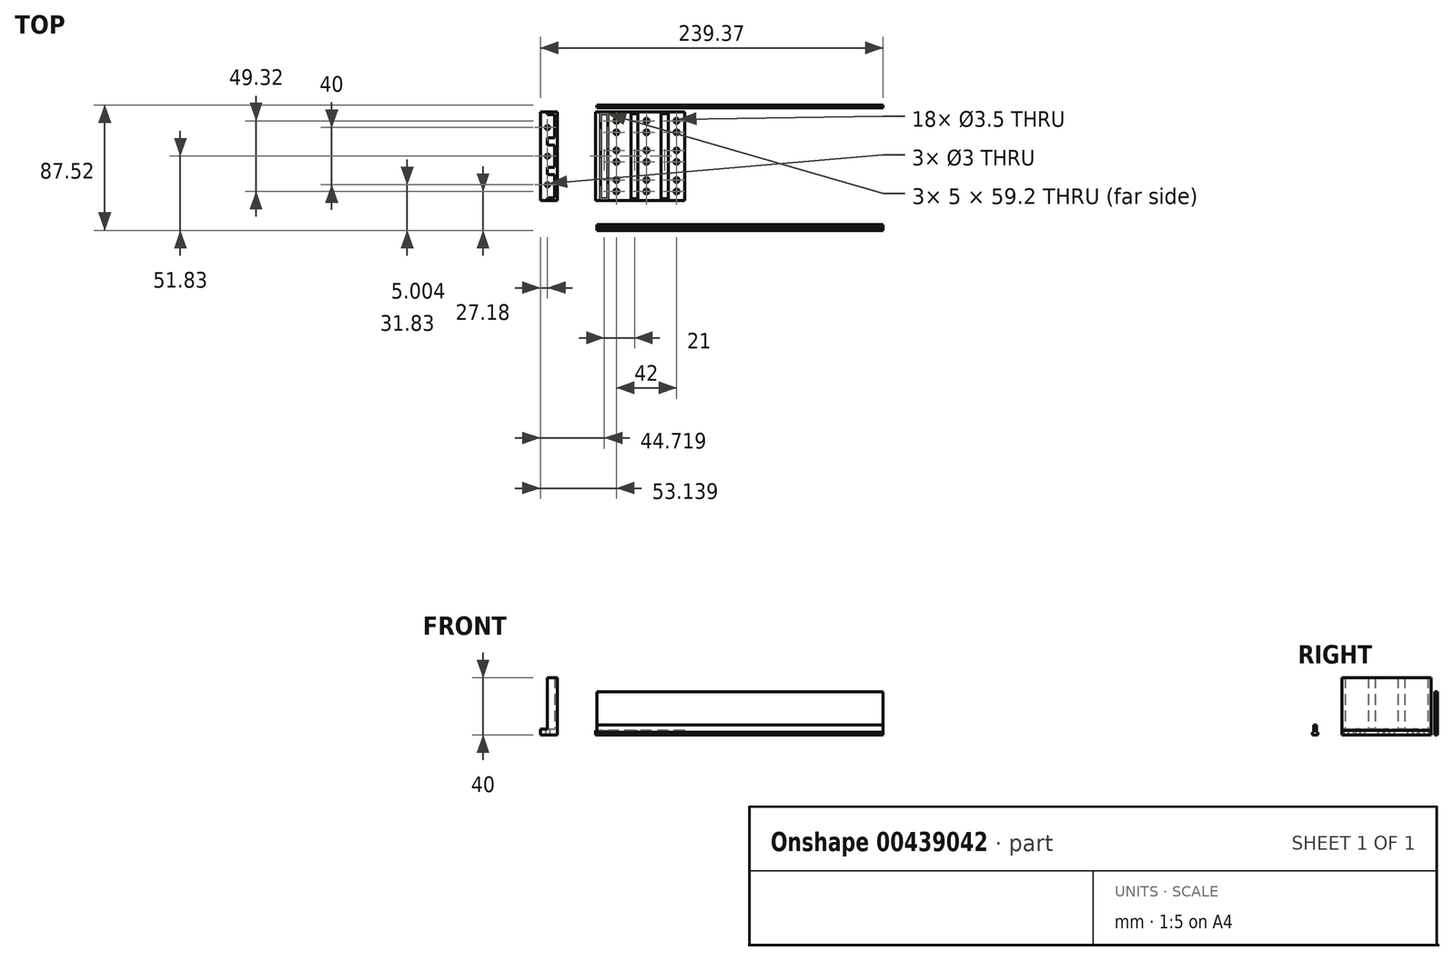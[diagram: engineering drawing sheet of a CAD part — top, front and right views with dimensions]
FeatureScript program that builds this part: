
annotation { "Feature Type Name" : "Feature", "Feature Type Description" : "" }
export const myFeature = defineFeature(function(context is Context, id is Id, definition is map)
    precondition{}
    {
        {
            var Q0;
            Q0=qCreatedBy(makeId("Top.planeOp"),FACE);
            var sketch = newSketch(context, id + "F0", { "sketchPlane" : qUnion([Q0])});
            skLineSegment(sketch, "E0.bottom", {"start": v(-38.73, -31) * mm, "end": v(-100.73, -31) * mm});
            skLineSegment(sketch, "E0.top", {"start": v(-38.73, 31) * mm, "end": v(-100.73, 31) * mm});
            skLineSegment(sketch, "E0.left", {"start": v(-38.73, -31) * mm, "end": v(-38.73, 31) * mm});
            skLineSegment(sketch, "E0.right", {"start": v(-100.73, -31) * mm, "end": v(-100.73, 31) * mm});
            skPoint(sketch, "E0.middle", {"position": v(-69.73, 0) * mm});
            skSolve(sketch);
        }
        {
            var Q0;
            Q0=qSketchRegion(id+"F0",true);
            extrude(context, id + "F1", {"entities" : qUnion([Q0]), "depth" : 3 * mm});
        }
        {
            var Q0;
            Q0=makeQuery(id+"F1.opExtrude","CAP_FACE",FACE,{"disambiguationData":[OSD([sQuery(id+"F0.wireOp",EDGE,"E0.bottom"),sQuery(id+"F0.wireOp",EDGE,"E0.top"),sQuery(id+"F0.wireOp",EDGE,"E0.left"),sQuery(id+"F0.wireOp",EDGE,"E0.right")])],"isStart":false});
            var sketch = newSketch(context, id + "F2", { "sketchPlane" : qUnion([Q0])});
            skCircle(sketch, "E1", {"center": v(-86.23, 24.67) * mm, "radius": 1.75 * mm});
            skCircle(sketch, "E2", {"center": v(-86.23, 16.67) * mm, "radius": 1.75 * mm});
            skCircle(sketch, "E3.0.1.0", {"center": v(-86.23, 4) * mm, "radius": 1.75 * mm});
            skCircle(sketch, "E3.0.1.1", {"center": v(-86.23, -4) * mm, "radius": 1.75 * mm});
            skCircle(sketch, "E3.0.2.0", {"center": v(-86.23, -16.65) * mm, "radius": 1.75 * mm});
            skCircle(sketch, "E3.0.2.1", {"center": v(-86.23, -24.65) * mm, "radius": 1.75 * mm});
            skCircle(sketch, "E3.1.0.0", {"center": v(-65.23, 24.67) * mm, "radius": 1.75 * mm});
            skCircle(sketch, "E3.1.0.1", {"center": v(-65.23, 16.67) * mm, "radius": 1.75 * mm});
            skCircle(sketch, "E3.1.1.0", {"center": v(-65.23, 4) * mm, "radius": 1.75 * mm});
            skCircle(sketch, "E3.1.1.1", {"center": v(-65.23, -4) * mm, "radius": 1.75 * mm});
            skCircle(sketch, "E3.1.2.0", {"center": v(-65.23, -16.65) * mm, "radius": 1.75 * mm});
            skCircle(sketch, "E3.1.2.1", {"center": v(-65.23, -24.65) * mm, "radius": 1.75 * mm});
            skCircle(sketch, "E3.2.0.0", {"center": v(-44.23, 24.67) * mm, "radius": 1.75 * mm});
            skCircle(sketch, "E3.2.0.1", {"center": v(-44.23, 16.67) * mm, "radius": 1.75 * mm});
            skCircle(sketch, "E3.2.1.0", {"center": v(-44.23, 4) * mm, "radius": 1.75 * mm});
            skCircle(sketch, "E3.2.1.1", {"center": v(-44.23, -4) * mm, "radius": 1.75 * mm});
            skCircle(sketch, "E3.2.2.0", {"center": v(-44.23, -16.65) * mm, "radius": 1.75 * mm});
            skCircle(sketch, "E3.2.2.1", {"center": v(-44.23, -24.65) * mm, "radius": 1.75 * mm});
            skLineSegment(sketch, "E3.direction1", {"start": v(-86.23, 16.67) * mm, "end": v(-65.23, 16.67) * mm, "construction": true});
            skLineSegment(sketch, "E3.direction2", {"start": v(-86.23, 16.67) * mm, "end": v(-86.23, -4) * mm, "construction": true});
            skLineSegment(sketch, "E4.bottom", {"start": v(-97.15, 29.6) * mm, "end": v(-92.15, 29.6) * mm});
            skLineSegment(sketch, "E4.top", {"start": v(-97.15, -29.6) * mm, "end": v(-92.15, -29.6) * mm});
            skLineSegment(sketch, "E4.left", {"start": v(-97.15, 29.6) * mm, "end": v(-97.15, -29.6) * mm});
            skLineSegment(sketch, "E4.right", {"start": v(-92.15, 29.6) * mm, "end": v(-92.15, -29.6) * mm});
            skLineSegment(sketch, "E5.1.0.0", {"start": v(-76.15, -29.6) * mm, "end": v(-71.15, -29.6) * mm});
            skLineSegment(sketch, "E5.1.0.1", {"start": v(-76.15, 29.6) * mm, "end": v(-71.15, 29.6) * mm});
            skLineSegment(sketch, "E5.1.0.2", {"start": v(-76.15, 29.6) * mm, "end": v(-76.15, -29.6) * mm});
            skLineSegment(sketch, "E5.1.0.3", {"start": v(-71.15, 29.6) * mm, "end": v(-71.15, -29.6) * mm});
            skLineSegment(sketch, "E5.2.0.0", {"start": v(-55.15, -29.6) * mm, "end": v(-50.15, -29.6) * mm});
            skLineSegment(sketch, "E5.2.0.1", {"start": v(-55.15, 29.6) * mm, "end": v(-50.15, 29.6) * mm});
            skLineSegment(sketch, "E5.2.0.2", {"start": v(-55.15, 29.6) * mm, "end": v(-55.15, -29.6) * mm});
            skLineSegment(sketch, "E5.2.0.3", {"start": v(-50.15, 29.6) * mm, "end": v(-50.15, -29.6) * mm});
            skLineSegment(sketch, "E5.direction1", {"start": v(-97.15, -29.6) * mm, "end": v(-76.15, -29.6) * mm, "construction": true});
            skSolve(sketch);
        }
        {
            var Q0;
            Q0=qSketchRegion(id+"F2",true);
            extrude(context, id + "F3", {"entities" : qUnion([Q0]), "operationType" : NewBodyOperationType.REMOVE, "oppositeDirection" : true, "depth" : 25 * mm});
        }
        {
            var Q0;
            Q0=qCreatedBy(makeId("Top.planeOp"),FACE);
            var sketch = newSketch(context, id + "F4", { "sketchPlane" : qUnion([Q0])});
            skLineSegment(sketch, "E6.bottom", {"start": v(-129.37, -31) * mm, "end": v(-139.37, -31) * mm});
            skLineSegment(sketch, "E6.top", {"start": v(-129.37, 31) * mm, "end": v(-139.37, 31) * mm});
            skLineSegment(sketch, "E6.left", {"start": v(-129.37, -31) * mm, "end": v(-129.37, 31) * mm});
            skLineSegment(sketch, "E6.right", {"start": v(-139.37, -31) * mm, "end": v(-139.37, 31) * mm});
            skPoint(sketch, "E6.middle", {"position": v(-134.37, 0) * mm});
            skCircle(sketch, "E7", {"center": v(-134.37, 20) * mm, "radius": 1.5 * mm});
            skCircle(sketch, "E8", {"center": v(-134.37, 0) * mm, "radius": 1.5 * mm});
            skCircle(sketch, "E9", {"center": v(-134.37, -20) * mm, "radius": 1.5 * mm});
            skSolve(sketch);
        }
        {
            var Q0;
            Q0=qSketchRegion(id+"F4",true);
            extrude(context, id + "F5", {"entities" : qUnion([Q0]), "depth" : 4 * mm});
        }
        {
            var Q0;
            Q0=qCreatedBy(makeId("Top.planeOp"),FACE);
            var sketch = newSketch(context, id + "F6", { "sketchPlane" : qUnion([Q0])});
            skLineSegment(sketch, "E10.bottom", {"start": v(-127.37, -31) * mm, "end": v(-129.37, -31) * mm});
            skLineSegment(sketch, "E10.top", {"start": v(-127.37, 31) * mm, "end": v(-129.37, 31) * mm});
            skLineSegment(sketch, "E10.left", {"start": v(-127.37, -31) * mm, "end": v(-127.37, 31) * mm});
            skLineSegment(sketch, "E10.right", {"start": v(-129.37, -31) * mm, "end": v(-129.37, 31) * mm});
            skPoint(sketch, "E10.middle", {"position": v(-128.37, 0) * mm});
            skLineSegment(sketch, "E11.bottom", {"start": v(-129.37, 31) * mm, "end": v(-134.37, 31) * mm});
            skLineSegment(sketch, "E11.top", {"start": v(-129.37, 29) * mm, "end": v(-134.37, 29) * mm});
            skLineSegment(sketch, "E11.left", {"start": v(-129.37, 31) * mm, "end": v(-129.37, 29) * mm});
            skLineSegment(sketch, "E11.right", {"start": v(-134.37, 31) * mm, "end": v(-134.37, 29) * mm});
            skLineSegment(sketch, "E12.bottom", {"start": v(-129.37, -31) * mm, "end": v(-134.37, -31) * mm});
            skLineSegment(sketch, "E12.top", {"start": v(-129.37, -29) * mm, "end": v(-134.37, -29) * mm});
            skLineSegment(sketch, "E12.left", {"start": v(-129.37, -31) * mm, "end": v(-129.37, -29) * mm});
            skLineSegment(sketch, "E12.right", {"start": v(-134.37, -31) * mm, "end": v(-134.37, -29) * mm});
            skLineSegment(sketch, "E13.bottom", {"start": v(-129.37, 7.84) * mm, "end": v(-134.37, 7.84) * mm});
            skLineSegment(sketch, "E13.top", {"start": v(-129.37, 12.84) * mm, "end": v(-134.37, 12.84) * mm});
            skLineSegment(sketch, "E13.left", {"start": v(-129.37, 7.84) * mm, "end": v(-129.37, 12.84) * mm});
            skLineSegment(sketch, "E13.right", {"start": v(-134.37, 7.84) * mm, "end": v(-134.37, 12.84) * mm});
            skPoint(sketch, "E13.middle", {"position": v(-131.87, 10.34) * mm});
            skLineSegment(sketch, "E14.bottom", {"start": v(-129.37, -12.82) * mm, "end": v(-134.37, -12.82) * mm});
            skLineSegment(sketch, "E14.top", {"start": v(-129.37, -7.82) * mm, "end": v(-134.37, -7.82) * mm});
            skLineSegment(sketch, "E14.left", {"start": v(-129.37, -12.82) * mm, "end": v(-129.37, -7.82) * mm});
            skLineSegment(sketch, "E14.right", {"start": v(-134.37, -12.82) * mm, "end": v(-134.37, -7.82) * mm});
            skPoint(sketch, "E14.middle", {"position": v(-131.87, -10.32) * mm});
            skSolve(sketch);
        }
        {
            var Q0;
            Q0=qSketchRegion(id+"F6",true);
            extrude(context, id + "F7", {"entities" : qUnion([Q0]), "operationType" : NewBodyOperationType.ADD, "depth" : 40 * mm});
        }
        {
            var Q0;
            Q0=qCreatedBy(makeId("Top.planeOp"),FACE);
            var sketch = newSketch(context, id + "F8", { "sketchPlane" : qUnion([Q0])});
            skLineSegment(sketch, "E15.bottom", {"start": v(100, 33.69) * mm, "end": v(-100, 33.69) * mm});
            skLineSegment(sketch, "E15.top", {"start": v(100, 35.69) * mm, "end": v(-100, 35.69) * mm});
            skLineSegment(sketch, "E15.left", {"start": v(100, 33.69) * mm, "end": v(100, 35.69) * mm});
            skLineSegment(sketch, "E15.right", {"start": v(-100, 33.69) * mm, "end": v(-100, 35.69) * mm});
            skPoint(sketch, "E15.middle", {"position": v(0, 34.69) * mm});
            skSolve(sketch);
        }
        {
            var Q0;
            Q0=qSketchRegion(id+"F8",true);
            extrude(context, id + "F9", {"entities" : qUnion([Q0]), "depth" : 30 * mm});
        }
        {
            var Q0;
            Q0=qCreatedBy(makeId("Top.planeOp"),FACE);
            var sketch = newSketch(context, id + "F10", { "sketchPlane" : qUnion([Q0])});
            skLineSegment(sketch, "E16.bottom", {"start": v(100, -47.83) * mm, "end": v(-100, -47.83) * mm});
            skLineSegment(sketch, "E16.top", {"start": v(100, -51.83) * mm, "end": v(-100, -51.83) * mm});
            skLineSegment(sketch, "E16.left", {"start": v(100, -47.83) * mm, "end": v(100, -51.83) * mm});
            skLineSegment(sketch, "E16.right", {"start": v(-100, -47.83) * mm, "end": v(-100, -51.83) * mm});
            skPoint(sketch, "E16.middle", {"position": v(0, -49.83) * mm});
            skSolve(sketch);
        }
        {
            var Q0;
            Q0=qSketchRegion(id+"F10",true);
            extrude(context, id + "F11", {"entities" : qUnion([Q0]), "depth" : 2 * mm});
        }
        {
            var Q0;
            Q0=makeQuery(id+"F11.opExtrude","CAP_FACE",FACE,{"disambiguationData":[OSD([sQuery(id+"F10.wireOp",EDGE,"E16.bottom"),sQuery(id+"F10.wireOp",EDGE,"E16.top"),sQuery(id+"F10.wireOp",EDGE,"E16.left"),sQuery(id+"F10.wireOp",EDGE,"E16.right")])],"isStart":false});
            var sketch = newSketch(context, id + "F12", { "sketchPlane" : qUnion([Q0])});
            skLineSegment(sketch, "E17.bottom", {"start": v(100, -50.83) * mm, "end": v(-100, -50.83) * mm});
            skLineSegment(sketch, "E17.top", {"start": v(100, -48.83) * mm, "end": v(-100, -48.83) * mm});
            skLineSegment(sketch, "E17.left", {"start": v(100, -50.83) * mm, "end": v(100, -48.83) * mm});
            skLineSegment(sketch, "E17.right", {"start": v(-100, -50.83) * mm, "end": v(-100, -48.83) * mm});
            skPoint(sketch, "E17.middle", {"position": v(0, -49.83) * mm});
            skSolve(sketch);
        }
        {
            var Q0;
            Q0=qSketchRegion(id+"F12",true);
            extrude(context, id + "F13", {"entities" : qUnion([Q0]), "operationType" : NewBodyOperationType.ADD, "depth" : 5 * mm});
        }
    });
